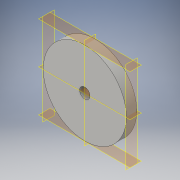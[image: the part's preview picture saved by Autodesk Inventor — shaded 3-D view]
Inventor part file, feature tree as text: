
AUTODESK INVENTOR PART (.ipt)
format: ipt  version: 2016 (Build 200138000, 138)  size: 98,816 bytes
history: native  units: in
note: dims shown in document units (in); Inventor stores cm internally (conversion verified against a paired STEP export)
features: plane x4, extrude x1, sketch x1
ambient origin geometry x8: Origin, YZ Plane, XZ Plane, XY Plane, X Axis, Y Axis, Z Axis, Center Point
bodies: Solid1 (feature_tree)
feature tree (6):
  extrude  "Extrusion1"  Depth=2.0in
  plane  "Work Plane1"
  plane  "Work Plane2"
  plane  "Work Plane3"
  plane  "Work Plane4"
  sketch  "Sketch1"  dims[d0=0.5in d1=4.0in d2=0.5in d3=0.0in d4=2.0in d5=-2.0in d6=2.0in d7=-2.0in]
